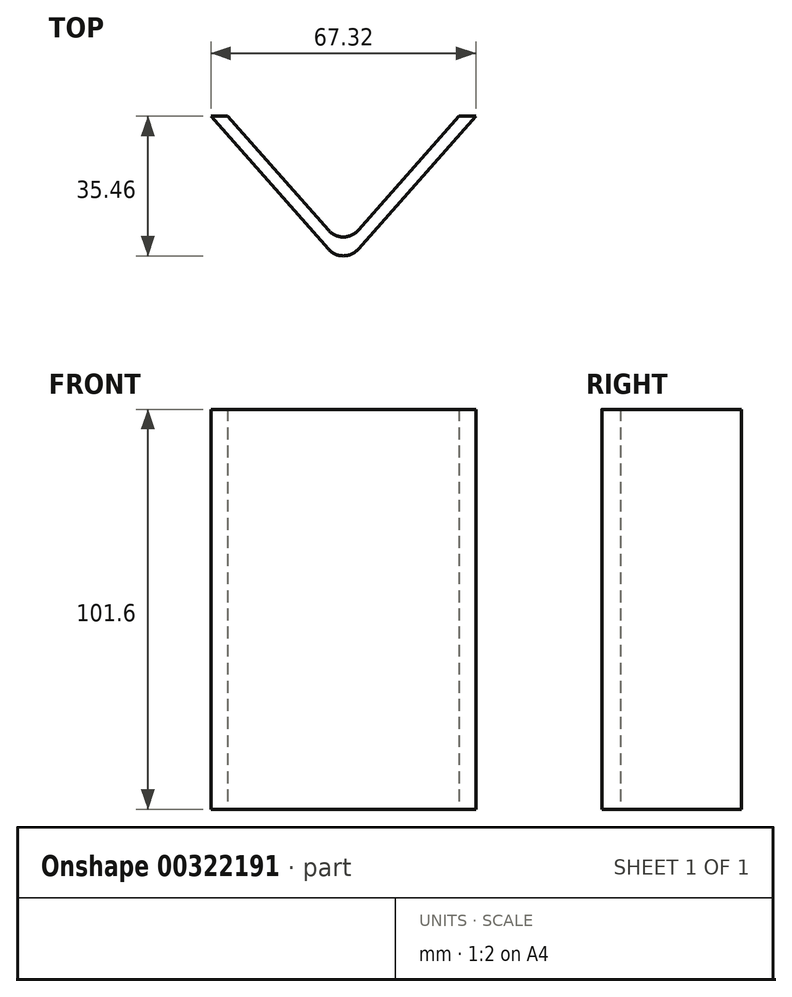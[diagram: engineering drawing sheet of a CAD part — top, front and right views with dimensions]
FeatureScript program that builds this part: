
annotation { "Feature Type Name" : "Feature", "Feature Type Description" : "" }
export const myFeature = defineFeature(function(context is Context, id is Id, definition is map)
    precondition{}
    {
        {
            var Q0;
            Q0=qCreatedBy(makeId("Top.planeOp"),FACE);
            var sketch = newSketch(context, id + "F0", { "sketchPlane" : qUnion([Q0])});
            skLineSegment(sketch, "E0", {"start": v(0, -38.05) * mm, "end": v(33.66, 0) * mm});
            skLineSegment(sketch, "E1", {"start": v(-33.66, 0) * mm, "end": v(0, -38.05) * mm});
            skLineSegment(sketch, "E2", {"start": v(-33.66, 0) * mm, "end": v(-29.42, 0) * mm});
            skLineSegment(sketch, "E3", {"start": v(0, -33.25) * mm, "end": v(29.42, 0) * mm});
            skLineSegment(sketch, "E4", {"start": v(0, -33.25) * mm, "end": v(-29.42, 0) * mm});
            skLineSegment(sketch, "E5", {"start": v(29.42, 0) * mm, "end": v(33.66, 0) * mm});
            skSolve(sketch);
        }
        {
            var Q0;
            Q0 = qSketchRegion(id + "F0", true);
            extrude(context, id + "F1", {"entities" : qUnion([Q0]), "depth" : 101.6 * mm});
        }
        {
            var Q0;
            Q0=makeQuery(id+"F1.opExtrude","SWEPT_EDGE",EDGE,{"disambiguationData":[OSD([sQuery(id+"F0.wireOp",EDGE,"E3"),sQuery(id+"F0.wireOp",EDGE,"E4")])]});
            fillet(context, id + "F2", {"entities" : qUnion([Q0]), "radius" : 5.08 * mm, "tangentPropagation" : true, "allowEdgeOverflow" : false});
        }
        {
            var Q0;
            Q0=makeQuery(id+"F6HFOZQrpjhMcN5_1.boolean.opBoolean","SPLIT",EDGE,{"derivedFrom":makeQuery(id+"F1.opExtrude","SWEPT_EDGE",EDGE,{"disambiguationData":[OSD([sQuery(id+"F0.wireOp",EDGE,"E0"),sQuery(id+"F0.wireOp",EDGE,"E1")])]})});
            fillet(context, id + "F3", {"entities" : qUnion([Q0]), "radius" : 5.08 * mm, "tangentPropagation" : true, "allowEdgeOverflow" : false});
        }
    });
